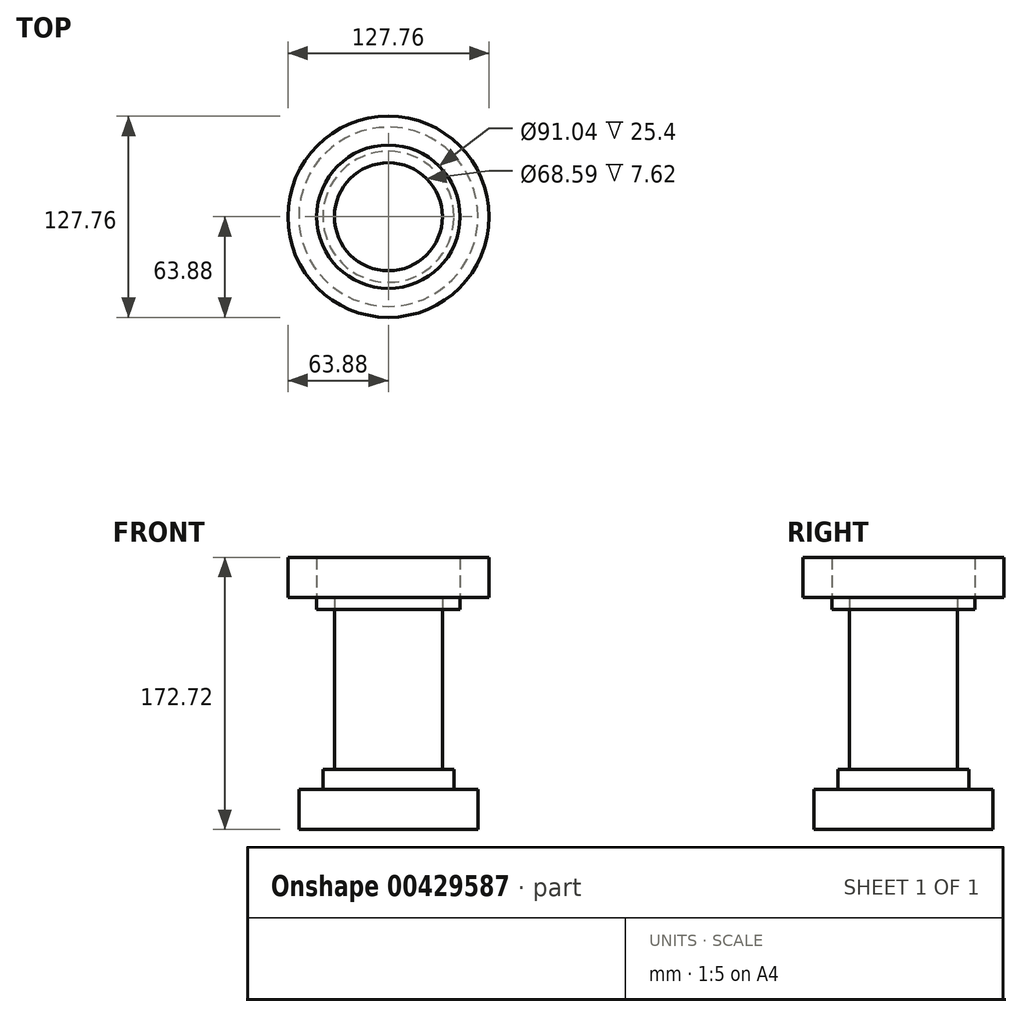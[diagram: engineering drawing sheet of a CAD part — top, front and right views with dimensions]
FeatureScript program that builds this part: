
annotation { "Feature Type Name" : "Feature", "Feature Type Description" : "" }
export const myFeature = defineFeature(function(context is Context, id is Id, definition is map)
    precondition{}
    {
        {
            var Q0;
            Q0=qCreatedBy(makeId("Top.planeOp"),FACE);
            var sketch = newSketch(context, id + "F0", { "sketchPlane" : qUnion([Q0])});
            skCircle(sketch, "E0", {"center": v(0, 0) * mm, "radius": 56.91 * mm});
            skSolve(sketch);
        }
        {
            var Q0;
            Q0 = qSketchRegion(id + "F0", true);
            extrude(context, id + "F1", {"entities" : qUnion([Q0]), "depth" : 25.4 * mm});
        }
        {
            var Q0;
            Q0=makeQuery(id+"F1.opExtrude","CAP_FACE",FACE,{"disambiguationData":[OSD([sQuery(id+"F0.wireOp",EDGE,"E0")])],"isStart":false});
            var sketch = newSketch(context, id + "F2", { "sketchPlane" : qUnion([Q0])});
            skCircle(sketch, "E1", {"center": v(0, 0) * mm, "radius": 41.62 * mm});
            skSolve(sketch);
        }
        {
            var Q0;
            Q0 = qSketchRegion(id + "F2", true);
            extrude(context, id + "F3", {"entities" : qUnion([Q0]), "operationType" : NewBodyOperationType.ADD, "depth" : 12.7 * mm});
        }
        {
            var Q0;
            Q0=makeQuery(id+"F3.opExtrude","CAP_FACE",FACE,{"disambiguationData":[OSD([sQuery(id+"F2.wireOp",EDGE,"E1")])],"isStart":false});
            var sketch = newSketch(context, id + "F4", { "sketchPlane" : qUnion([Q0])});
            skCircle(sketch, "E2", {"center": v(0, 0) * mm, "radius": 34.3 * mm});
            skSolve(sketch);
        }
        {
            var Q0;
            Q0 = qSketchRegion(id + "F4", true);
            extrude(context, id + "F5", {"entities" : qUnion([Q0]), "operationType" : NewBodyOperationType.ADD, "depth" : 101.6 * mm});
        }
        {
            var Q0;
            Q0=makeQuery(id+"F5.opExtrude","CAP_FACE",FACE,{"disambiguationData":[OSD([sQuery(id+"F4.wireOp",EDGE,"E2")])],"isStart":false});
            var sketch = newSketch(context, id + "F6", { "sketchPlane" : qUnion([Q0])});
            skCircle(sketch, "E3", {"center": v(0, 0) * mm, "radius": 45.52 * mm});
            skSolve(sketch);
        }
        {
            var Q0;
            Q0=makeQuery(id+"F6.imprint","IMPRINT",FACE,{"disambiguationData":[TD([[makeQuery(id+"F6.imprint","IMPRINT",EDGE,{"derivedFrom":sQuery(id+"F6.wireOp",EDGE,"E3")}),1.0]])]});
            extrude(context, id + "F7", {"entities" : qUnion([Q0]), "depth" : 7.62 * mm});
        }
        {
            var Q0;
            Q0=makeQuery(id+"F7.opExtrude","CAP_FACE",FACE,{"disambiguationData":[OSD([sQuery(id+"F4.wireOp",EDGE,"E2"),sQuery(id+"F6.wireOp",EDGE,"E3")])],"isStart":false});
            var sketch = newSketch(context, id + "F8", { "sketchPlane" : qUnion([Q0])});
            skCircle(sketch, "E4", {"center": v(0, 0) * mm, "radius": 63.88 * mm});
            skSolve(sketch);
        }
        {
            var Q0;
            Q0=makeQuery(id+"F8.imprint","IMPRINT",FACE,{"disambiguationData":[TD([[makeQuery(id+"F8.imprint","IMPRINT",EDGE,{"derivedFrom":sQuery(id+"F8.wireOp",EDGE,"E4")}),1.0]])]});
            extrude(context, id + "F9", {"entities" : qUnion([Q0]), "depth" : 25.4 * mm});
        }
    });
